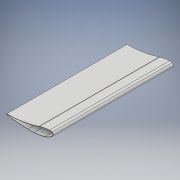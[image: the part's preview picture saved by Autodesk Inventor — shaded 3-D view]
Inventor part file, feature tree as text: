
AUTODESK INVENTOR PART (.ipt)
format: ipt  version: 2018.2 (Build 222227000, 227)  size: 128,512 bytes
history: native  units: mm
features: extrude x1, shell x1, sketch x1, projected_geometry x1
ambient origin geometry x8: Origin, YZ Plane, XZ Plane, XY Plane, X Axis, Y Axis, Z Axis, Center Point
bodies: Body1 (feature_tree)
feature tree (4):
  extrude  "押し出し1"  Depth=946.0mm TaperAngle=0.0deg
  shell  "シェル1"  Thickness=3.0mm
  sketch  "スケッチ1"
  projected_geometry  "投影ループ1"
